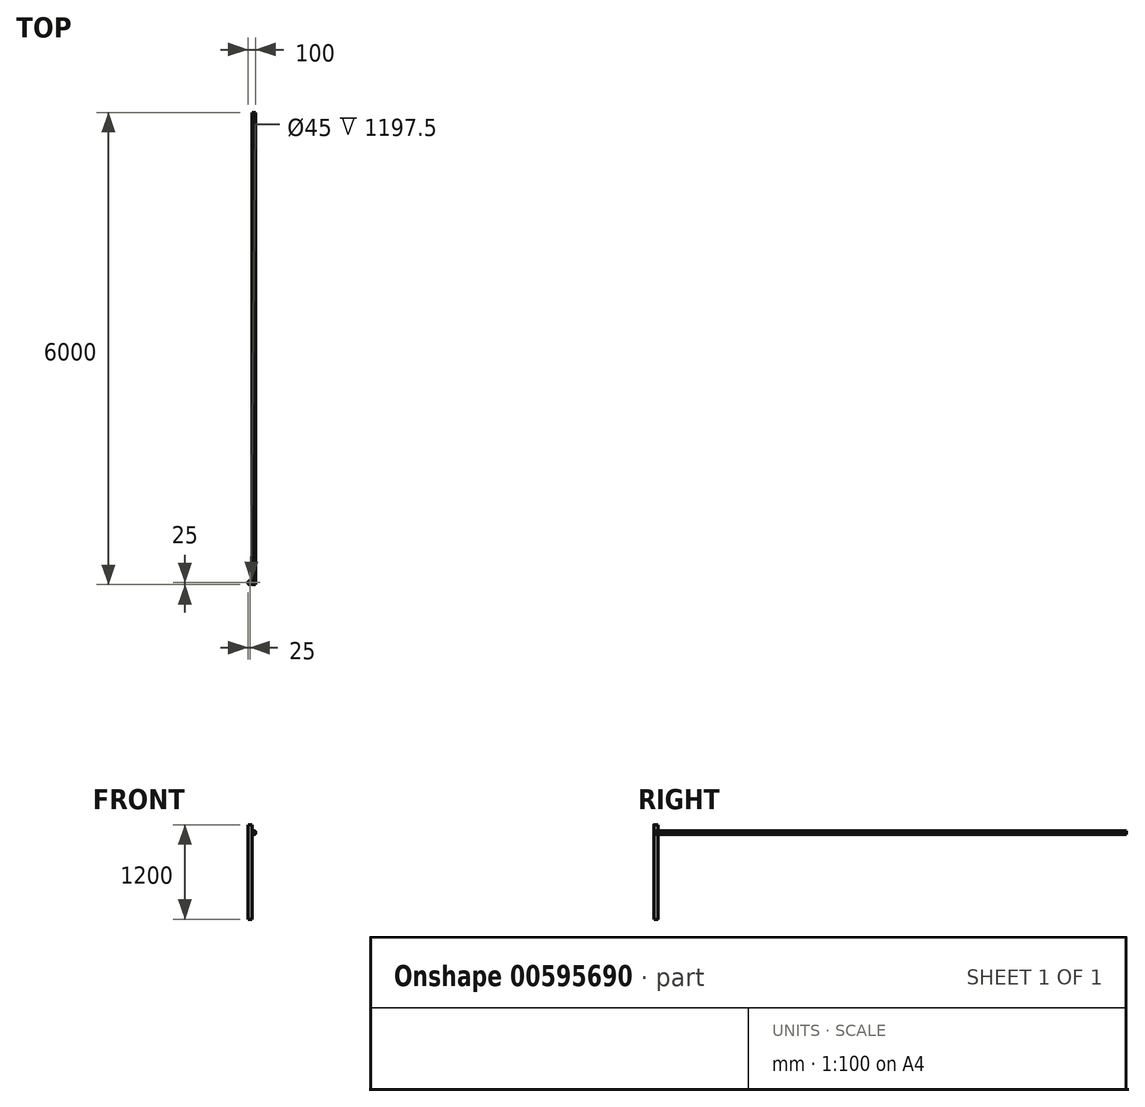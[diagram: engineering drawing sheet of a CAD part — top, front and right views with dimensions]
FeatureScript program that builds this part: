
annotation { "Feature Type Name" : "Feature", "Feature Type Description" : "" }
export const myFeature = defineFeature(function(context is Context, id is Id, definition is map)
    precondition{}
    {
        {
            var Q0;
            Q0=qCreatedBy(makeId("Top.planeOp"),FACE);
            var sketch = newSketch(context, id + "F0", { "sketchPlane" : qUnion([Q0])});
            skCircle(sketch, "E0", {"center": v(0, 0) * mm, "radius": 25 * mm});
            skSolve(sketch);
        }
        {
            var Q0;
            Q0=makeQuery(id+"F0.imprint","IMPRINT",FACE,{"disambiguationData":[TD([[makeQuery(id+"F0.imprint","IMPRINT",EDGE,{"derivedFrom":sQuery(id+"F0.wireOp",EDGE,"E0")}),1.0]])]});
            extrude(context, id + "F1", {"entities" : qUnion([Q0]), "endBound" : BoundingType.SYMMETRIC, "depth" : 1200 * mm, "offsetDistance" : 25 * mm});
        }
        {
            var Q0;
            Q0=makeQuery(id+"F1.opExtrude","CAP_FACE",FACE,{"disambiguationData":[OSD([sQuery(id+"F0.wireOp",EDGE,"E0")])],"isStart":false});
            shell(context, id + "F2", {"entities" : qUnion([Q0]), "thickness" : 2.5 * mm});
        }
        {
            var Q0;
            Q0=qCreatedBy(makeId("Front.planeOp"),FACE);
            cPlane(context, id + "F3", {"entities" : qUnion([Q0]), "cplaneType" : CPlaneType.OFFSET, "offset" : 25 * mm, "width" : 150 * mm, "height" : 150 * mm});
        }
        {
            var Q0;
            Q0=qCreatedBy(id+"F3.planeOp",FACE);
            var sketch = newSketch(context, id + "F4", { "sketchPlane" : qUnion([Q0])});
            skCircle(sketch, "E1", {"center": v(50, 500) * mm, "radius": 25 * mm});
            skSolve(sketch);
        }
        {
            var Q0;
            Q0 = qSketchRegion(id + "F4", true);
            extrude(context, id + "F5", {"entities" : qUnion([Q0]), "oppositeDirection" : true, "depth" : 6000 * mm, "offsetDistance" : 25 * mm});
        }
    });
